# Revit family: Sink_Single_ Bowl_Wall_Hung-Elkay-EWS3120W4C_6C
name_source: partatom
category: Plumbing Fixtures
units: mm (PartAtom-declared; Revit-internal decimal feet)

## family parameters
Cut with Voids When Loaded = No
Host = Face
Maintain Annotation Orientation = No
OmniClass Number = 23.45.05.14.14
OmniClass Title = Sinks/Lavatories
Part Type = Normal
Room Calculation Point = No
Round Connector Dimension = Use Diameter
Shared = No

## types (2) — shared parameters
Activation Method = Manually Operated
Approx. Shipping Weight (lbs) = 50
Assembly Code = D2010400
Back Splash Height = 6 "
Bowl 1 Dimensions = 28 inch x 16 inch x 10 1/2 inch
CWFU = 1
Default Elevation = 48 "
Description = Stainless Steel 31 inch x 19 1/2 inch x 10 1/2 inch Wall Hung Single Bowl Hand Wash Sink Kit
Drain Location = Rear Center
Drain Size = 3.5 "
Drainboard Location = No drainboard
Faucet Hole Size = 1.5 "
Flow Rate (GPM) = 2 GPM
HWFU = 1
Inlet Connection Size (inch) = 0.5 "
Installation Type = Wall Hung
Main Material = Finish-Elkay-Stainless Steel
Manufacturer = Elkay Manufacturer Company
Manufacturer Brand = Elkay (by Zurn Elkay Water Solutions)
Material_Blue = Finish-Elkay-Blue
Material_Red = Finish-Elkay-Red
No of Bowls = 1
Outlet Connection Size (inch) = 1.5 "
Product Documentation Link = https://www.elkayfiles.com
Product Installation Sheet URL = https://www.elkayfiles.com
Product Page URL = https://www.elkay.com
Product Weight (lbs) = 48
Product data URL = https://www.bimobject.com
Repair Parts URL = https://www.elkayfiles.com
Sink Dimensions = 31 inch x 19 1/2 inch x 24 3/8 inch
Spout Height = 11 "
Spout Reach = 5.13 "
Spout Type = Gooseneck
URL = https://www.elkay.com
zero-valued in all types: WFU

## per-type parameters (varying)
| type | Model |
| EWS3120W6C (Wall Hung Single Bowl Hand Wash Sink Kit ) | EWS3120W6C |
| EWS3120W4C (Wall Hung Single Bowl Hand Wash Sink Kit ) | EWS3120W4C |

## geometry (parser evidence)
native form markers: Blend x4, Sweep x11
no freeform markers — native parametric forms only
